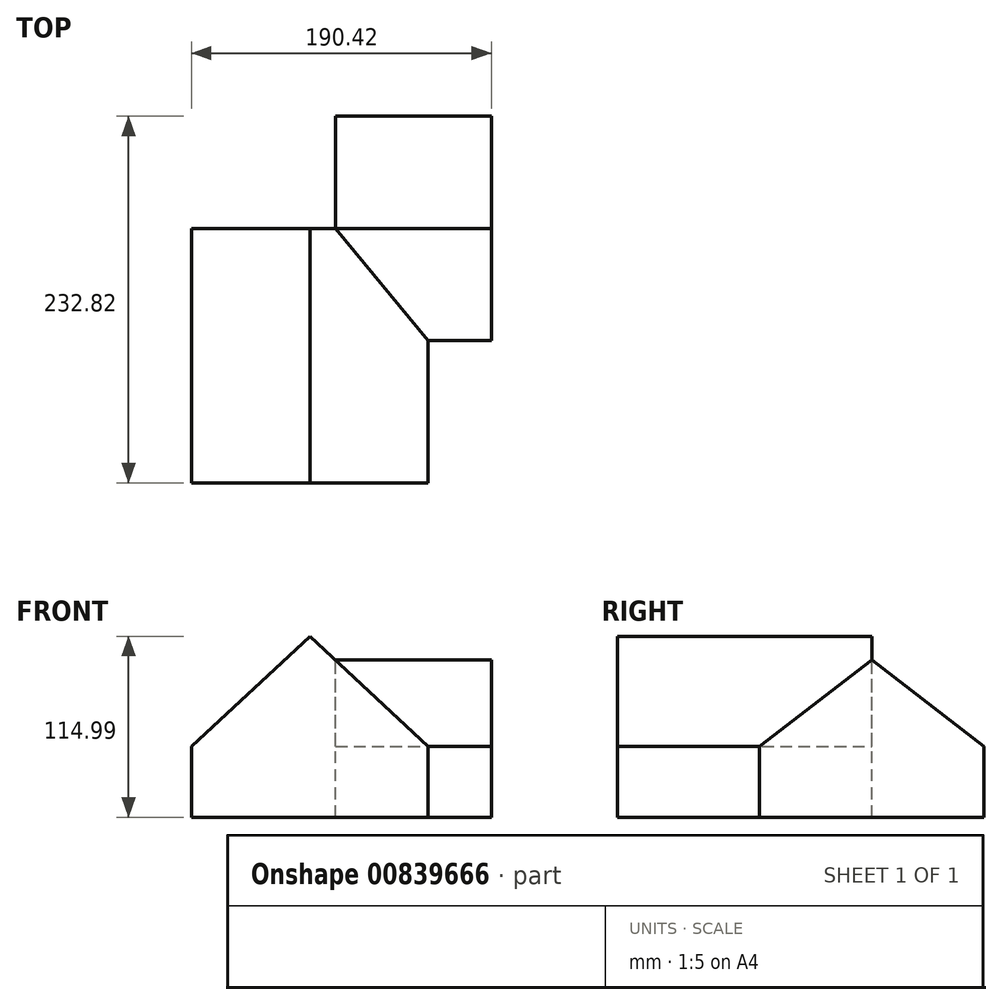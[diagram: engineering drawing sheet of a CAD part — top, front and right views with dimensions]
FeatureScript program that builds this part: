
annotation { "Feature Type Name" : "Feature", "Feature Type Description" : "" }
export const myFeature = defineFeature(function(context is Context, id is Id, definition is map)
    precondition{}
    {
        {
            var Q0;
            Q0=qCreatedBy(makeId("Front.planeOp"),FACE);
            var sketch = newSketch(context, id + "F0", { "sketchPlane" : qUnion([Q0])});
            skLineSegment(sketch, "E0.bottom", {"start": v(0, 0) * mm, "end": v(150.29, 0) * mm});
            skLineSegment(sketch, "E0.top", {"start": v(0, 44.92) * mm, "end": v(150.29, 44.92) * mm});
            skLineSegment(sketch, "E0.left", {"start": v(0, 0) * mm, "end": v(0, 44.92) * mm});
            skLineSegment(sketch, "E0.right", {"start": v(150.29, 0) * mm, "end": v(150.29, 44.92) * mm});
            skLineSegment(sketch, "E1", {"start": v(0, 44.92) * mm, "end": v(75.14, 115) * mm});
            skPoint(sketch, "E1.endSnap0", {"position": v(75.14, 44.92) * mm});
            skLineSegment(sketch, "E2", {"start": v(75.14, 115) * mm, "end": v(150.29, 44.92) * mm});
            skSolve(sketch);
        }
        {
            var Q0;
            Q0 = qSketchRegion(id + "F0", true);
            extrude(context, id + "F1", {"entities" : qUnion([Q0]), "depth" : 161.55 * mm, "offsetDistance" : 25 * mm});
        }
        {
            var Q0;
            Q0=qCreatedBy(makeId("Right.planeOp"),FACE);
            var sketch = newSketch(context, id + "F2", { "sketchPlane" : qUnion([Q0])});
            skLineSegment(sketch, "E3.bottom", {"start": v(-71.27, 0) * mm, "end": v(71.27, 0) * mm});
            skLineSegment(sketch, "E3.top", {"start": v(-71.27, 44.92) * mm, "end": v(71.27, 44.92) * mm});
            skLineSegment(sketch, "E3.left", {"start": v(-71.27, 0) * mm, "end": v(-71.27, 44.92) * mm});
            skLineSegment(sketch, "E3.right", {"start": v(71.27, 0) * mm, "end": v(71.27, 44.92) * mm});
            skLineSegment(sketch, "E4", {"start": v(71.27, 44.92) * mm, "end": v(0, 99.81) * mm});
            skLineSegment(sketch, "E5", {"start": v(0, 99.81) * mm, "end": v(-71.27, 44.92) * mm});
            skSolve(sketch);
        }
        {
            var Q0;
            Q0=qCreatedBy(makeId("Right.planeOp"),FACE);
            cPlane(context, id + "F3", {"entities" : qUnion([Q0]), "cplaneType" : CPlaneType.OFFSET, "offset" : 190.42 * mm, "width" : 150 * mm, "height" : 150 * mm});
        }
        {
            var Q0;
            Q0=qCreatedBy(id+"F3.planeOp",FACE);
            var sketch = newSketch(context, id + "F4", { "sketchPlane" : qUnion([Q0])});
            skLineSegment(sketch, "E6.0.0", {"start": v(71.27, 44.92) * mm, "end": v(-71.27, 44.92) * mm});
            skLineSegment(sketch, "E6.0.1", {"start": v(-71.27, 44.92) * mm, "end": v(-71.27, 0) * mm});
            skLineSegment(sketch, "E6.0.2", {"start": v(-71.27, 0) * mm, "end": v(71.27, 0) * mm});
            skLineSegment(sketch, "E6.0.3", {"start": v(71.27, 0) * mm, "end": v(71.27, 44.92) * mm});
            skLineSegment(sketch, "E7.0.0", {"start": v(0, 99.81) * mm, "end": v(-71.27, 44.92) * mm});
            skLineSegment(sketch, "E7.0.1", {"start": v(-71.27, 44.92) * mm, "end": v(71.27, 44.92) * mm});
            skLineSegment(sketch, "E7.0.2", {"start": v(71.27, 44.92) * mm, "end": v(0, 99.81) * mm});
            skSolve(sketch);
        }
        {
            var Q0;
            Q0 = qSketchRegion(id + "F4", true);
            extrude(context, id + "F5", {"entities" : qUnion([Q0]), "operationType" : NewBodyOperationType.ADD, "oppositeDirection" : true, "depth" : 98.83 * mm, "offsetDistance" : 25 * mm});
        }
    });
